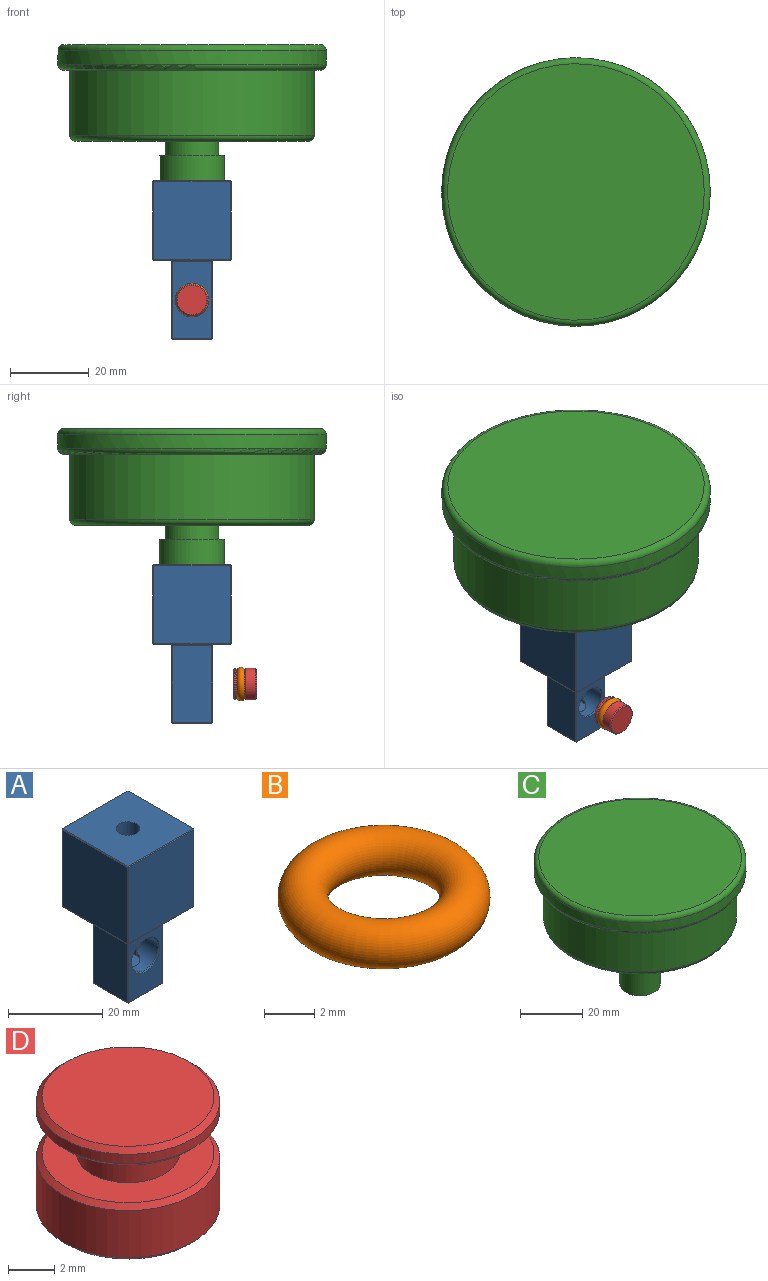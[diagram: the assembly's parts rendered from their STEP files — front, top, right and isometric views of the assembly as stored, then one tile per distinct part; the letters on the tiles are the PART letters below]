
ASSEMBLY  parts=4 mates=3
PART A: 58 faces, bbox 20x20x40.3 mm
  f0: plane 19.5x19.5mm, normal (0,0,-1), area 259.8mm2, adj f18,f19,f20,f21,f25,f26,f27,f30
  f1: plane 6.25x1.5mm, normal (0,-1,0), area 6.5mm2, adj f12,f15
  f2: plane 19.75x19.5mm, normal (0,1,0), area 385.1mm2, adj f44,f45,f53,f54
  f3: plane 19.75x19.5mm, normal (-1,0,0), area 385.1mm2, adj f43,f52,f53,f57
  f4: plane 19.75x19.5mm, normal (0,-1,0), area 385.1mm2, adj f41,f42,f51,f52
  f5: plane 19.75x19.5mm, normal (1,0,0), area 385.1mm2, adj f38,f41,f45,f46
  f6: plane 19.5x19.5mm, normal (0,0,1), area 360.6mm2, adj f15,f46,f51,f54,f57
  f7: plane 19.5x10mm, normal (1,0,0), area 195mm2, adj f21,f22,f31,f32
  f8: plane 19.5x10mm, normal (0,-1,0), area 138.3mm2, adj f17,f26,f31,f34,f37
  f9: plane 19.5x10mm, normal (-1,0,0), area 195mm2, adj f24,f25,f33,f34
  f10: plane 19.5x10mm, normal (0,1,0), area 195mm2, adj f18,f22,f23,f24
  f11: plane 10x10mm, normal (0,0,-1), area 100mm2, adj f23,f32,f33,f37
  f12: cylinder r=4mm len=8mm, axis (0,-1,0), area 104.9mm2, adj f1,f13,f14,f15,f17
  f13: plane 6.25x1.5mm, normal (0,-1,0), area 6.5mm2, adj f12,f15
  f14: cylinder r=2.5mm len=2.5mm, axis (0,0,1), area 1.7mm2, adj f12,f15,f16
  f15: cylinder r=2.5mm len=34.25mm, axis (0,0,1), area 480.2mm2, adj f1,f6,f12,f13,f14,f16
  f16: plane 5x5mm, normal (0,0,1), area 19.6mm2, adj f14,f15
  f17: cone r=4mm half-angle=45deg, axis (0,-1,0), area 9.2mm2, adj f8,f12
  f18: plane 10x0.25mm, normal (0,0.71,-0.71), area 3.5mm2, adj f0,f10,f19,f20
  f19: plane 0.5x0.5mm, normal (0.58,0.58,-0.58), area 0.2mm2, adj f0,f18,f21,f22
  f20: plane 0.5x0.5mm, normal (-0.58,0.58,-0.58), area 0.2mm2, adj f0,f18,f24,f25
  f21: plane 10x0.25mm, normal (0.71,0,-0.71), area 3.5mm2, adj f0,f7,f19,f27
  f22: plane 19.5x0.25mm, normal (0.71,0.71,0), area 6.9mm2, adj f7,f10,f19,f28
  f23: plane 10x0.25mm, normal (0,0.71,-0.71), area 3.5mm2, adj f10,f11,f28,f29
  f24: plane 19.5x0.25mm, normal (-0.71,0.71,0), area 6.9mm2, adj f9,f10,f20,f29
  f25: plane 10x0.25mm, normal (-0.71,0,-0.71), area 3.5mm2, adj f0,f9,f20,f30
  f26: plane 10x0.25mm, normal (0,-0.71,-0.71), area 3.5mm2, adj f0,f8,f27,f30
  f27: plane 0.5x0.5mm, normal (0.58,-0.58,-0.58), area 0.2mm2, adj f0,f21,f26,f31
  f28: plane 0.25x0.25mm, normal (0.58,0.58,-0.58), area 0.1mm2, adj f22,f23,f32
  f29: plane 0.25x0.25mm, normal (-0.58,0.58,-0.58), area 0.1mm2, adj f23,f24,f33
  f30: plane 0.5x0.5mm, normal (-0.58,-0.58,-0.58), area 0.2mm2, adj f0,f25,f26,f34
  f31: plane 19.5x0.25mm, normal (0.71,-0.71,0), area 6.9mm2, adj f7,f8,f27,f35
  f32: plane 10x0.25mm, normal (0.71,0,-0.71), area 3.5mm2, adj f7,f11,f28,f35
  f33: plane 10x0.25mm, normal (-0.71,0,-0.71), area 3.5mm2, adj f9,f11,f29,f36
  f34: plane 19.5x0.25mm, normal (-0.71,-0.71,0), area 6.9mm2, adj f8,f9,f30,f36
  f35: plane 0.25x0.25mm, normal (0.58,-0.58,-0.58), area 0.1mm2, adj f31,f32,f37
  f36: plane 0.25x0.25mm, normal (-0.58,-0.58,-0.58), area 0.1mm2, adj f33,f34,f37
  f37: plane 10x0.25mm, normal (0,-0.71,-0.71), area 3.5mm2, adj f8,f11,f35,f36
  f38: plane 19.5x0.25mm, normal (0.71,0,-0.71), area 6.9mm2, adj f0,f5,f39,f40
  f39: plane 0.25x0.25mm, normal (0.58,-0.58,-0.58), area 0.1mm2, adj f38,f41,f42
  f40: plane 0.25x0.25mm, normal (0.58,0.58,-0.58), area 0.1mm2, adj f38,f44,f45
  f41: plane 19.75x0.25mm, normal (0.71,-0.71,0), area 7mm2, adj f4,f5,f39,f47
  f42: plane 19.5x0.25mm, normal (0,-0.71,-0.71), area 6.9mm2, adj f0,f4,f39,f48
  f43: plane 19.5x0.25mm, normal (-0.71,0,-0.71), area 6.9mm2, adj f0,f3,f48,f49
  f44: plane 19.5x0.25mm, normal (0,0.71,-0.71), area 6.9mm2, adj f0,f2,f40,f49
  f45: plane 19.75x0.25mm, normal (0.71,0.71,0), area 7mm2, adj f2,f5,f40,f50
  f46: plane 19.5x0.25mm, normal (0.71,0,0.71), area 6.9mm2, adj f5,f6,f47,f50
  f47: plane 0.25x0.25mm, normal (0.58,-0.58,0.58), area 0.1mm2, adj f41,f46,f51
  f48: plane 0.25x0.25mm, normal (-0.58,-0.58,-0.58), area 0.1mm2, adj f42,f43,f52
  f49: plane 0.25x0.25mm, normal (-0.58,0.58,-0.58), area 0.1mm2, adj f43,f44,f53
  f50: plane 0.25x0.25mm, normal (0.58,0.58,0.58), area 0.1mm2, adj f45,f46,f54
  f51: plane 19.5x0.25mm, normal (0,-0.71,0.71), area 6.9mm2, adj f4,f6,f47,f55
  f52: plane 19.75x0.25mm, normal (-0.71,-0.71,0), area 7mm2, adj f3,f4,f48,f55
  f53: plane 19.75x0.25mm, normal (-0.71,0.71,0), area 7mm2, adj f2,f3,f49,f56
  f54: plane 19.5x0.25mm, normal (0,0.71,0.71), area 6.9mm2, adj f2,f6,f50,f56
  f55: plane 0.25x0.25mm, normal (-0.58,-0.58,0.58), area 0.1mm2, adj f51,f52,f57
  f56: plane 0.25x0.25mm, normal (-0.58,0.58,0.58), area 0.1mm2, adj f53,f54,f57
  f57: plane 19.5x0.25mm, normal (-0.71,0,0.71), area 6.9mm2, adj f3,f6,f55,f56
PART B: 1 faces, bbox 9.2x9.2x2 mm
  f0: torus R=3.24mm, axis (0,0,-1), area 127.9mm2
PART C: 14 faces, bbox 73.6x73.6x49.8 mm
  f0: cylinder r=34mm len=68mm, axis (0,0,1), area 747.7mm2, adj f11,f13
  f1: plane 65x65mm, normal (0,0,1), area 3318.3mm2, adj f11
  f2: plane 13x13mm, normal (0,0,-1), area 132.7mm2, adj f3
  f3: cylinder r=6.5mm len=15.25mm, axis (0,0,1), area 622.8mm2, adj f2,f4
  f4: plane 16.5x16.5mm, normal (0,0,-1), area 81.1mm2, adj f3,f5
  f5: cylinder r=8.25mm len=16.5mm, axis (0,0,1), area 336.9mm2, adj f4,f6
  f6: plane 16.5x16.5mm, normal (0,0,1), area 70.7mm2, adj f5,f7
  f7: cylinder r=6.75mm len=13.5mm, axis (0,0,1), area 148.4mm2, adj f6,f8
  f8: plane 59x59mm, normal (0,0,-1), area 2590.8mm2, adj f7,f12
  f9: cylinder r=31mm len=62mm, axis (0,0,1), area 3213.8mm2, adj f10,f12
  f10: plane 65x65mm, normal (0,0,-1), area 299.2mm2, adj f9,f13
  f11: torus R=32.5mm, axis (0,0,1), area 495.3mm2, adj f0,f1
  f12: torus R=29.5mm, axis (0,0,1), area 450.9mm2, adj f8,f9
  f13: torus R=32.5mm, axis (0,0,-1), area 495.3mm2, adj f0,f10
PART D: 11 faces, bbox 8x8x6 mm
  f0: cylinder r=3.99mm len=7.98mm, axis (0,0,-1), area 62.7mm2, adj f7,f8
  f1: plane 7.48x7.48mm, normal (0,0,-1), area 43.9mm2, adj f8
  f2: cylinder r=2.24mm len=4.48mm, axis (0,0,-1), area 28.1mm2, adj f3,f4
  f3: plane 7.48x7.48mm, normal (0,0,1), area 28.2mm2, adj f2,f7
  f4: plane 7.48x7.48mm, normal (0,0,-1), area 28.2mm2, adj f2,f9
  f5: plane 7.48x7.48mm, normal (0,0,1), area 43.9mm2, adj f10
  f6: cylinder r=3.99mm len=7.98mm, axis (0,0,-1), area 12.5mm2, adj f9,f10
  f7: cone r=3.99mm half-angle=45deg, axis (0,0,-1), area 8.6mm2, adj f0,f3
  f8: cone r=3.99mm half-angle=45deg, axis (0,0,1), area 8.6mm2, adj f0,f1
  f9: cone r=3.74mm half-angle=45deg, axis (0,0,1), area 8.6mm2, adj f4,f6
  f10: cone r=3.74mm half-angle=45deg, axis (0,0,-1), area 8.6mm2, adj f5,f6
PLACE A t=(-23.43,-27.6,33.51)mm
PLACE B rot(axis=(-1,0,0),90deg) t=(-85.77,-41.13,-31.24)mm
PLACE C t=(-23.43,-27.6,33.51)mm
PLACE D rot(axis=(-1,0,0),90deg) t=(-73.43,-44,-31.24)mm
MATE fastened C.f0 <-> A.f14  axis (0,0,-1) through (-23.43,-27.6,-0.99)mm
MATE revolute B.f0 <-> D.f2  axis (0,-1,0) through (-23.43,-40,-31.24)mm
MATE cylindrical D.f0 <-> A.f12  axis (0,1,0) through (-23.43,-38,-31.24)mm
